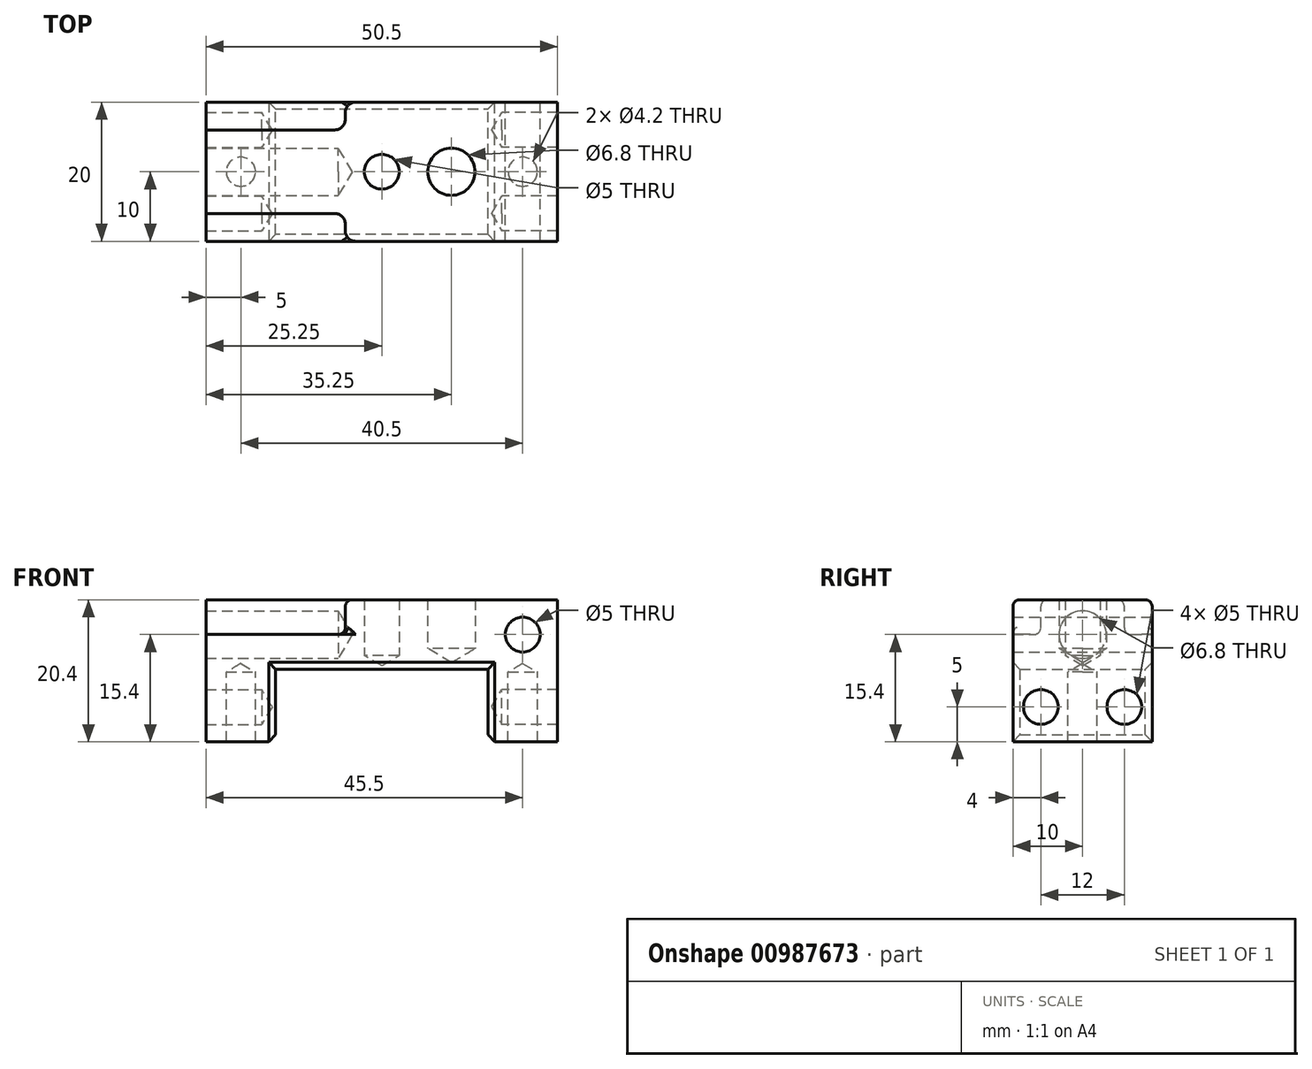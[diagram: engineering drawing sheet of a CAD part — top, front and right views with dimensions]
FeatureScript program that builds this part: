
annotation { "Feature Type Name" : "Feature", "Feature Type Description" : "" }
export const myFeature = defineFeature(function(context is Context, id is Id, definition is map)
    precondition{}
    {
        {
            var Q0;
            Q0=qCreatedBy(makeId("Front.planeOp"),FACE);
            var sketch = newSketch(context, id + "F0", { "sketchPlane" : qUnion([Q0])});
            skLineSegment(sketch, "E0", {"start": v(-25.25, -20.4) * mm, "end": v(-25.25, 0) * mm});
            skLineSegment(sketch, "E1", {"start": v(-25.25, 0) * mm, "end": v(25.25, 0) * mm});
            skLineSegment(sketch, "E2", {"start": v(25.25, 0) * mm, "end": v(25.25, -20.4) * mm});
            skLineSegment(sketch, "E3", {"start": v(25.25, -20.4) * mm, "end": v(15.25, -20.4) * mm});
            skLineSegment(sketch, "E4", {"start": v(15.25, -20.4) * mm, "end": v(15.25, -10) * mm});
            skLineSegment(sketch, "E5", {"start": v(15.25, -10) * mm, "end": v(-15.25, -10) * mm});
            skLineSegment(sketch, "E6", {"start": v(-15.25, -10) * mm, "end": v(-15.25, -20.4) * mm});
            skLineSegment(sketch, "E7", {"start": v(-15.25, -20.4) * mm, "end": v(-25.25, -20.4) * mm});
            skSolve(sketch);
        }
        {
            var Q0;
            Q0=makeQuery(id+"F0.imprint","IMPRINT",FACE,{"disambiguationData":[TD([[makeQuery(id+"F0.imprint","IMPRINT",EDGE,{"derivedFrom":sQuery(id+"F0.wireOp",EDGE,"E0")}),-1.0]])]});
            extrude(context, id + "F1", {"entities" : qUnion([Q0]), "depth" : 20 * mm, "offsetDistance" : 25 * mm, "symmetric" : true});
        }
        {
            var Q0;
            Q0=makeQuery(id+"F1.opExtrude","SWEPT_FACE",FACE,{"disambiguationData":[OSD([sQuery(id+"F0.wireOp",EDGE,"E0")])]});
            var sketch = newSketch(context, id + "F2", { "sketchPlane" : qUnion([Q0])});
            skPoint(sketch, "E8", {"position": v(-6, -15.4) * mm});
            skPoint(sketch, "E9", {"position": v(0, -15.4) * mm});
            skPoint(sketch, "E10", {"position": v(6, -15.4) * mm});
            skPoint(sketch, "E11", {"position": v(-6, -5) * mm});
            skPoint(sketch, "E12", {"position": v(0, -5) * mm});
            skPoint(sketch, "E13", {"position": v(6, -5) * mm});
            skSolve(sketch);
        }
        {
            var Q0;
            Q0=makeQuery(id+"F1.opExtrude","SWEPT_FACE",FACE,{"disambiguationData":[OSD([sQuery(id+"F0.wireOp",EDGE,"E0")])]});
            var sketch = newSketch(context, id + "F3", { "sketchPlane" : qUnion([Q0])});
            skPoint(sketch, "E14", {"position": v(-5, -5) * mm});
            skPoint(sketch, "E15", {"position": v(0, -5) * mm});
            skPoint(sketch, "E16", {"position": v(5, -5) * mm});
            skSolve(sketch);
        }
        {
            var Q0;
            Q0=makeQuery(id+"F1.opExtrude","SWEPT_FACE",FACE,{"disambiguationData":[OSD([sQuery(id+"F0.wireOp",EDGE,"E2")])]});
            var sketch = newSketch(context, id + "F4", { "sketchPlane" : qUnion([Q0])});
            skPoint(sketch, "E17", {"position": v(-6, -15.4) * mm});
            skPoint(sketch, "E18", {"position": v(6, -15.4) * mm});
            skSolve(sketch);
        }
        {
            var Q0;
            Q0=sQuery(id+"F2.wireOp",VERTEX,"E10");
            var Q1;
            Q1=sQuery(id+"F2.wireOp",VERTEX,"E8");
            var Q2;
            Q2=sQuery(id+"F4.wireOp",VERTEX,"E17");
            var Q3;
            Q3=sQuery(id+"F4.wireOp",VERTEX,"E18");
            var Q4;
            Q4=makeQuery(id+"F1.opExtrude","SWEPT_BODY",BODY,{"disambiguationData":[OSD([sQuery(id+"F0.wireOp",EDGE,"E0"),sQuery(id+"F0.wireOp",EDGE,"E1"),sQuery(id+"F0.wireOp",EDGE,"E2"),sQuery(id+"F0.wireOp",EDGE,"E3"),sQuery(id+"F0.wireOp",EDGE,"E4"),sQuery(id+"F0.wireOp",EDGE,"E5"),sQuery(id+"F0.wireOp",EDGE,"E6"),sQuery(id+"F0.wireOp",EDGE,"E7")])]});
            hole(context, id + "F5", {"style" : HoleStyle.SIMPLE, "endStyle" : HoleEndStyle.BLIND, "standardTappedOrClearance" : lookupTablePath({ "standard" : "ISO", "engagement" : "75%", "pitch" : "1 mm", "size" : "M6", "type" : "Tapped" }), "standardBlindInLast" : lookupTablePath({ "standard" : "ISO", "fit" : "Normal", "engagement" : "75%", "pitch" : "1 mm", "size" : "M6", "type" : "Clearance & tapped" }), "holeDiameter" : 5 * mm, "majorDiameter" : 6 * mm, "showTappedDepth" : true, "holeDepth" : 8 * mm, "isTappedThrough" : true, "tappedDepth" : 7 * mm, "tapClearance" : 1, "locations" : qUnion([Q0, Q1, Q2, Q3]), "scope" : qUnion([Q4]), "startStyle" : HoleStartStyle.PART});
        }
        {
            var Q0;
            Q0=sQuery(id+"F3.wireOp",VERTEX,"E15");
            var Q1;
            Q1=makeQuery(id+"F1.opExtrude","SWEPT_BODY",BODY,{"disambiguationData":[OSD([sQuery(id+"F0.wireOp",EDGE,"E0"),sQuery(id+"F0.wireOp",EDGE,"E1"),sQuery(id+"F0.wireOp",EDGE,"E2"),sQuery(id+"F0.wireOp",EDGE,"E3"),sQuery(id+"F0.wireOp",EDGE,"E4"),sQuery(id+"F0.wireOp",EDGE,"E5"),sQuery(id+"F0.wireOp",EDGE,"E6"),sQuery(id+"F0.wireOp",EDGE,"E7")])]});
            hole(context, id + "F6", {"style" : HoleStyle.SIMPLE, "endStyle" : HoleEndStyle.BLIND, "standardTappedOrClearance" : lookupTablePath({ "standard" : "ISO", "engagement" : "75%", "pitch" : "1.25 mm", "size" : "M8", "type" : "Tapped" }), "standardBlindInLast" : lookupTablePath({ "standard" : "ISO", "fit" : "Normal", "engagement" : "75%", "pitch" : "1.25 mm", "size" : "M8", "type" : "Clearance & tapped" }), "holeDiameter" : 6.8 * mm, "majorDiameter" : 8 * mm, "showTappedDepth" : true, "holeDepth" : 19 * mm, "isTappedThrough" : true, "tappedDepth" : 17.75 * mm, "tapClearance" : 1, "locations" : qUnion([Q0]), "scope" : qUnion([Q1]), "startStyle" : HoleStartStyle.PART});
        }
        {
            var Q0;
            Q0=makeQuery(id+"F1.opExtrude","SWEPT_FACE",FACE,{"disambiguationData":[OSD([sQuery(id+"F0.wireOp",EDGE,"E7")])]});
            var sketch = newSketch(context, id + "F7", { "sketchPlane" : qUnion([Q0])});
            skPoint(sketch, "E19", {"position": v(-20.25, 0) * mm});
            skPoint(sketch, "E20", {"position": v(20.25, 0) * mm});
            skSolve(sketch);
        }
        {
            var Q0;
            Q0=sQuery(id+"F7.wireOp",VERTEX,"E19");
            var Q1;
            Q1=sQuery(id+"F7.wireOp",VERTEX,"e6091487-3df0-4c40-86b1-ffb490b8e503");
            var Q2;
            Q2=sQuery(id+"F7.wireOp",VERTEX,"25d8340f-edf2-4a82-998f-7ccab65ba808");
            var Q3;
            Q3=sQuery(id+"F7.wireOp",VERTEX,"E20");
            var Q4;
            Q4=makeQuery(id+"F1.opExtrude","SWEPT_BODY",BODY,{"disambiguationData":[OSD([sQuery(id+"F0.wireOp",EDGE,"E0"),sQuery(id+"F0.wireOp",EDGE,"E1"),sQuery(id+"F0.wireOp",EDGE,"E2"),sQuery(id+"F0.wireOp",EDGE,"E3"),sQuery(id+"F0.wireOp",EDGE,"E4"),sQuery(id+"F0.wireOp",EDGE,"E5"),sQuery(id+"F0.wireOp",EDGE,"E6"),sQuery(id+"F0.wireOp",EDGE,"E7")])]});
            hole(context, id + "F8", {"style" : HoleStyle.SIMPLE, "endStyle" : HoleEndStyle.BLIND, "standardTappedOrClearance" : lookupTablePath({ "standard" : "ISO", "engagement" : "75%", "pitch" : "0.8 mm", "size" : "M5", "type" : "Tapped" }), "standardBlindInLast" : lookupTablePath({ "standard" : "ISO", "fit" : "Normal", "engagement" : "75%", "pitch" : "0.8 mm", "size" : "M5", "type" : "Clearance & tapped" }), "holeDiameter" : 4.2 * mm, "majorDiameter" : 5 * mm, "showTappedDepth" : true, "holeDepth" : 10 * mm, "isTappedThrough" : true, "tappedDepth" : 8.4 * mm, "tapClearance" : 2, "locations" : qUnion([Q0, Q1, Q2, Q3]), "scope" : qUnion([Q4]), "startStyle" : HoleStartStyle.PART});
        }
        {
            var Q0;
            Q0=makeQuery(id+"F1.opExtrude","CAP_FACE",FACE,{"disambiguationData":[OSD([sQuery(id+"F0.wireOp",EDGE,"E0"),sQuery(id+"F0.wireOp",EDGE,"E1"),sQuery(id+"F0.wireOp",EDGE,"E2"),sQuery(id+"F0.wireOp",EDGE,"E3"),sQuery(id+"F0.wireOp",EDGE,"E4"),sQuery(id+"F0.wireOp",EDGE,"E5"),sQuery(id+"F0.wireOp",EDGE,"E6"),sQuery(id+"F0.wireOp",EDGE,"E7")])],"isStart":false});
            var sketch = newSketch(context, id + "F9", { "sketchPlane" : qUnion([Q0])});
            skPoint(sketch, "E21", {"position": v(0, -5) * mm});
            skPoint(sketch, "E22", {"position": v(20.25, -5) * mm});
            skSolve(sketch);
        }
        {
            var Q0;
            Q0=sQuery(id+"F9.wireOp",VERTEX,"E22");
            var Q1;
            Q1=makeQuery(id+"F1.opExtrude","SWEPT_BODY",BODY,{"disambiguationData":[OSD([sQuery(id+"F0.wireOp",EDGE,"E0"),sQuery(id+"F0.wireOp",EDGE,"E1"),sQuery(id+"F0.wireOp",EDGE,"E2"),sQuery(id+"F0.wireOp",EDGE,"E3"),sQuery(id+"F0.wireOp",EDGE,"E4"),sQuery(id+"F0.wireOp",EDGE,"E5"),sQuery(id+"F0.wireOp",EDGE,"E6"),sQuery(id+"F0.wireOp",EDGE,"E7")])]});
            hole(context, id + "F10", {"style" : HoleStyle.SIMPLE, "endStyle" : HoleEndStyle.BLIND, "standardTappedOrClearance" : lookupTablePath({ "standard" : "ISO", "engagement" : "75%", "pitch" : "1 mm", "size" : "M6", "type" : "Tapped" }), "standardBlindInLast" : lookupTablePath({ "standard" : "ISO", "fit" : "Normal", "engagement" : "75%", "pitch" : "1 mm", "size" : "M6", "type" : "Clearance & tapped" }), "holeDiameter" : 5 * mm, "majorDiameter" : 6 * mm, "showTappedDepth" : true, "holeDepth" : 20 * mm, "isTappedThrough" : true, "tappedDepth" : 20 * mm, "tapClearance" : 0, "locations" : qUnion([Q0]), "scope" : qUnion([Q1]), "startStyle" : HoleStartStyle.PART});
        }
        {
            var Q0;
            Q0=makeQuery(id+"F1.opExtrude","SWEPT_FACE",FACE,{"disambiguationData":[OSD([sQuery(id+"F0.wireOp",EDGE,"E1")])]});
            var sketch = newSketch(context, id + "F11", { "sketchPlane" : qUnion([Q0])});
            skPoint(sketch, "E23", {"position": v(10, 0) * mm});
            skSolve(sketch);
        }
        {
            var Q0;
            Q0=makeQuery(id+"F1.opExtrude","SWEPT_FACE",FACE,{"disambiguationData":[OSD([sQuery(id+"F0.wireOp",EDGE,"E1")])]});
            var sketch = newSketch(context, id + "F12", { "sketchPlane" : qUnion([Q0])});
            skPoint(sketch, "E24", {"position": v(0, 0) * mm});
            skSolve(sketch);
        }
        {
            var Q0;
            Q0=sQuery(id+"F11.wireOp",VERTEX,"7e3da84f-6b7b-4d2c-855b-950176b45a1a");
            var Q1;
            Q1=sQuery(id+"F11.wireOp",VERTEX,"E23");
            var Q2;
            Q2=makeQuery(id+"F1.opExtrude","SWEPT_BODY",BODY,{"disambiguationData":[OSD([sQuery(id+"F0.wireOp",EDGE,"E0"),sQuery(id+"F0.wireOp",EDGE,"E1"),sQuery(id+"F0.wireOp",EDGE,"E2"),sQuery(id+"F0.wireOp",EDGE,"E3"),sQuery(id+"F0.wireOp",EDGE,"E4"),sQuery(id+"F0.wireOp",EDGE,"E5"),sQuery(id+"F0.wireOp",EDGE,"E6"),sQuery(id+"F0.wireOp",EDGE,"E7")])]});
            hole(context, id + "F13", {"style" : HoleStyle.SIMPLE, "endStyle" : HoleEndStyle.BLIND, "standardTappedOrClearance" : lookupTablePath({ "standard" : "ISO", "engagement" : "75%", "pitch" : "1.25 mm", "size" : "M8", "type" : "Tapped" }), "standardBlindInLast" : lookupTablePath({ "standard" : "ISO", "fit" : "Normal", "engagement" : "75%", "pitch" : "1.25 mm", "size" : "M8", "type" : "Clearance & tapped" }), "holeDiameter" : 6.8 * mm, "majorDiameter" : 8 * mm, "showTappedDepth" : true, "holeDepth" : 7 * mm, "isTappedThrough" : true, "tappedDepth" : 7 * mm, "tapClearance" : 0, "locations" : qUnion([Q0, Q1]), "scope" : qUnion([Q2]), "startStyle" : HoleStartStyle.PART});
        }
        {
            var Q0;
            Q0=sQuery(id+"F12.wireOp",VERTEX,"E24");
            var Q1;
            Q1=makeQuery(id+"F1.opExtrude","SWEPT_BODY",BODY,{"disambiguationData":[OSD([sQuery(id+"F0.wireOp",EDGE,"E0"),sQuery(id+"F0.wireOp",EDGE,"E1"),sQuery(id+"F0.wireOp",EDGE,"E2"),sQuery(id+"F0.wireOp",EDGE,"E3"),sQuery(id+"F0.wireOp",EDGE,"E4"),sQuery(id+"F0.wireOp",EDGE,"E5"),sQuery(id+"F0.wireOp",EDGE,"E6"),sQuery(id+"F0.wireOp",EDGE,"E7")])]});
            hole(context, id + "F14", {"style" : HoleStyle.SIMPLE, "endStyle" : HoleEndStyle.BLIND, "standardTappedOrClearance" : lookupTablePath({ "standard" : "ISO", "engagement" : "75%", "pitch" : "1 mm", "size" : "M6", "type" : "Tapped" }), "standardBlindInLast" : lookupTablePath({ "standard" : "ISO", "fit" : "Normal", "engagement" : "75%", "pitch" : "1 mm", "size" : "M6", "type" : "Clearance & tapped" }), "holeDiameter" : 5 * mm, "majorDiameter" : 6 * mm, "showTappedDepth" : true, "holeDepth" : 8 * mm, "tappedDepth" : 7 * mm, "tapClearance" : 1, "locations" : qUnion([Q0]), "scope" : qUnion([Q1]), "startStyle" : HoleStartStyle.PART});
        }
        {
            var Q0;
            Q0=makeQuery(id+"F1.opExtrude","SWEPT_FACE",FACE,{"disambiguationData":[OSD([sQuery(id+"F0.wireOp",EDGE,"E1")])]});
            var sketch = newSketch(context, id + "F15", { "sketchPlane" : qUnion([Q0])});
            skLineSegment(sketch, "E25", {"start": v(-25.25, -6) * mm, "end": v(-6.75, -6) * mm});
            skLineSegment(sketch, "E26", {"start": v(-5.25, -7.5) * mm, "end": v(-5.25, -8.5) * mm});
            skArc(sketch, "E27", {"start": v(-5.25, -7.5) * mm, "mid": v(-5.69, -6.44) * mm, "end": v(-6.75, -6) * mm});
            skLineSegment(sketch, "E28.MirrorCS", {"start": v(-25.25, 6) * mm, "end": v(-6.75, 6) * mm});
            skArc(sketch, "E29.MirrorCS", {"start": v(-5.25, 7.5) * mm, "mid": v(-5.69, 6.44) * mm, "end": v(-6.75, 6) * mm});
            skLineSegment(sketch, "E30.MirrorCS", {"start": v(-5.25, 7.5) * mm, "end": v(-5.25, 8.5) * mm});
            skArc(sketch, "E31", {"start": v(-3.75, 10) * mm, "mid": v(-4.81, 9.56) * mm, "end": v(-5.25, 8.5) * mm});
            skLineSegment(sketch, "E32.0", {"start": v(-25.25, 10) * mm, "end": v(-3.75, 10) * mm});
            skPoint(sketch, "E33.orphan", {"position": v(25.25, 10) * mm});
            skPoint(sketch, "E34.orphan", {"position": v(-5.25, 10) * mm});
            skArc(sketch, "E35", {"start": v(-5.25, -8.5) * mm, "mid": v(-4.81, -9.56) * mm, "end": v(-3.75, -10) * mm});
            skLineSegment(sketch, "E36.0", {"start": v(-25.25, -10) * mm, "end": v(-3.75, -10) * mm});
            skPoint(sketch, "E37.orphan", {"position": v(25.25, -10) * mm});
            skPoint(sketch, "E38.orphan", {"position": v(-5.25, -10) * mm});
            skLineSegment(sketch, "E39.0", {"start": v(-25.25, -10) * mm, "end": v(-25.25, -6) * mm});
            skLineSegment(sketch, "E40.trimOffspring", {"start": v(-25.25, 6) * mm, "end": v(-25.25, 10) * mm});
            skSolve(sketch);
        }
        {
            var Q0;
            {var subQ4=sQuery(id+"F15.wireOp",EDGE,"E25");Q0=makeQuery(id+"F15.imprint","IMPRINT",FACE,{"disambiguationData":[TD([[makeQuery(id+"F15.imprint","IMPRINT",EDGE,{"derivedFrom":subQ4}),-1.0]])]});}
            var Q1;
            {var subQ5=sQuery(id+"F15.wireOp",EDGE,"E28.MirrorCS");Q1=makeQuery(id+"F15.imprint","IMPRINT",FACE,{"disambiguationData":[TD([[makeQuery(id+"F15.imprint","IMPRINT",EDGE,{"derivedFrom":subQ5}),1.0]])]});}
            var Q2;
            {var subQ5=sQuery(id+"F15.wireOp",EDGE,"07d17622-57c3-4b9c-a85e-e3c76536f9360.MirrorCS");Q2=makeQuery(id+"F15.imprint","IMPRINT",FACE,{"disambiguationData":[TD([[makeQuery(id+"F15.imprint","IMPRINT",EDGE,{"derivedFrom":subQ5}),-1.0]])]});}
            var Q3;
            {var subQ5=sQuery(id+"F15.wireOp",EDGE,"14fbb9d8-2b5f-48ad-a6e9-3267166c27070.MirrorCS");Q3=makeQuery(id+"F15.imprint","IMPRINT",FACE,{"disambiguationData":[TD([[makeQuery(id+"F15.imprint","IMPRINT",EDGE,{"derivedFrom":subQ5}),1.0]])]});}
            extrude(context, id + "F16", {"entities" : qUnion([Q0, Q1, Q2, Q3]), "operationType" : NewBodyOperationType.REMOVE, "oppositeDirection" : true, "depth" : 5 * mm, "offsetDistance" : 25 * mm});
        }
        {
            var Q0;
            Q0=makeQuery(id+"F1.opExtrude","SWEPT_EDGE",EDGE,{"disambiguationData":[OSD([sQuery(id+"F0.wireOp",EDGE,"E3"),sQuery(id+"F0.wireOp",EDGE,"E4")])]});
            var Q1;
            Q1=makeQuery(id+"F1.opExtrude","SWEPT_EDGE",EDGE,{"disambiguationData":[OSD([sQuery(id+"F0.wireOp",EDGE,"E6"),sQuery(id+"F0.wireOp",EDGE,"E7")])]});
            var Q2;
            Q2=makeQuery(id+"F1.opExtrude","CAP_EDGE",EDGE,{"disambiguationData":[OSD([sQuery(id+"F0.wireOp",EDGE,"E6")])],"isStart":false});
            var Q3;
            Q3=makeQuery(id+"F1.opExtrude","CAP_EDGE",EDGE,{"disambiguationData":[OSD([sQuery(id+"F0.wireOp",EDGE,"E5")])],"isStart":false});
            var Q4;
            Q4=makeQuery(id+"F1.opExtrude","CAP_EDGE",EDGE,{"disambiguationData":[OSD([sQuery(id+"F0.wireOp",EDGE,"E4")])],"isStart":false});
            var Q5;
            Q5=makeQuery(id+"F1.opExtrude","CAP_EDGE",EDGE,{"disambiguationData":[OSD([sQuery(id+"F0.wireOp",EDGE,"E5")])],"isStart":true});
            var Q6;
            Q6=makeQuery(id+"F1.opExtrude","CAP_EDGE",EDGE,{"disambiguationData":[OSD([sQuery(id+"F0.wireOp",EDGE,"E6")])],"isStart":true});
            var Q7;
            Q7=makeQuery(id+"F1.opExtrude","CAP_EDGE",EDGE,{"disambiguationData":[OSD([sQuery(id+"F0.wireOp",EDGE,"E4")])],"isStart":true});
            chamfer(context, id + "F17", {"entities" : qUnion([Q0, Q1, Q2, Q3, Q4, Q5, Q6, Q7]), "width" : 1 * mm, "tangentPropagation" : true});
        }
        {
            var Q0;
            Q0=makeQuery(id+"F16.boolean.opBoolean","COPY",EDGE,{"derivedFrom":makeQuery(id+"F16.opExtrude","CAP_EDGE",EDGE,{"disambiguationData":[OSD([sQuery(id+"F15.wireOp",EDGE,"E25")])],"isStart":false})});
            var Q1;
            Q1=makeQuery(id+"F16.boolean.opBoolean","COPY",EDGE,{"derivedFrom":makeQuery(id+"F16.opExtrude","CAP_EDGE",EDGE,{"disambiguationData":[OSD([sQuery(id+"F15.wireOp",EDGE,"E28.MirrorCS")])],"isStart":false})});
            var Q2;
            Q2=makeQuery(id+"F1.opExtrude","CAP_EDGE",EDGE,{"disambiguationData":[OSD([sQuery(id+"F0.wireOp",EDGE,"E1")])],"isStart":false});
            var Q3;
            Q3=makeQuery(id+"F1.opExtrude","CAP_EDGE",EDGE,{"disambiguationData":[OSD([sQuery(id+"F0.wireOp",EDGE,"E1")])],"isStart":true});
            var Q4;
            Q4=makeQuery(id+"F16.boolean.opBoolean","COPY",EDGE,{"derivedFrom":makeQuery(id+"F16.opExtrude","CAP_EDGE",EDGE,{"disambiguationData":[OSD([sQuery(id+"F15.wireOp",EDGE,"E29.MirrorCS")])],"isStart":true})});
            var Q5;
            Q5=makeQuery(id+"F16.boolean.opBoolean","COPY",EDGE,{"derivedFrom":makeQuery(id+"F16.opExtrude","CAP_EDGE",EDGE,{"disambiguationData":[OSD([sQuery(id+"F15.wireOp",EDGE,"E26")])],"isStart":true})});
            fillet(context, id + "F18", {"entities" : qUnion([Q0, Q1, Q2, Q3, Q4, Q5]), "radius" : 1 * mm, "tangentPropagation" : true, "allowEdgeOverflow" : false});
        }
    });
